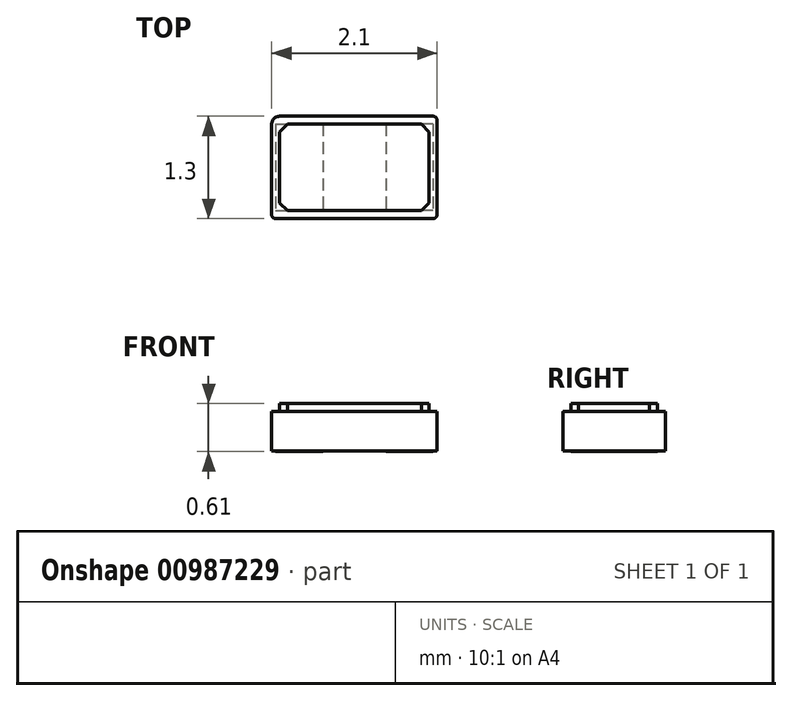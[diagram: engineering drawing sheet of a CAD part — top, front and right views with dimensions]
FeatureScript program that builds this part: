
annotation { "Feature Type Name" : "Feature", "Feature Type Description" : "" }
export const myFeature = defineFeature(function(context is Context, id is Id, definition is map)
    precondition{}
    {
        {
            var Q0;
            Q0=qCreatedBy(makeId("Top.planeOp"),FACE);
            var sketch = newSketch(context, id + "F0", { "sketchPlane" : qUnion([Q0])});
            skLineSegment(sketch, "E0.bottom", {"start": v(-0.95, 0.65) * mm, "end": v(1, 0.65) * mm});
            skLineSegment(sketch, "E0.top", {"start": v(-1, -0.65) * mm, "end": v(1, -0.65) * mm});
            skLineSegment(sketch, "E0.left", {"start": v(-1.05, 0.55) * mm, "end": v(-1.05, -0.6) * mm});
            skLineSegment(sketch, "E0.right", {"start": v(1.05, 0.6) * mm, "end": v(1.05, -0.6) * mm});
            skPoint(sketch, "E0.middle", {"position": v(0, 0) * mm});
            skPoint(sketch, "E1.visualSharp", {"position": v(-1.05, 0.65) * mm});
            skArc(sketch, "E1.filletArc", {"start": v(-0.95, 0.65) * mm, "mid": v(-1.02, 0.62) * mm, "end": v(-1.05, 0.55) * mm});
            skPoint(sketch, "E2.visualSharp", {"position": v(1.05, 0.65) * mm});
            skArc(sketch, "E2.filletArc", {"start": v(1.05, 0.6) * mm, "mid": v(1.04, 0.64) * mm, "end": v(1, 0.65) * mm});
            skPoint(sketch, "E3.visualSharp", {"position": v(-1.05, -0.65) * mm});
            skArc(sketch, "E3.filletArc", {"start": v(-1.05, -0.6) * mm, "mid": v(-1.04, -0.64) * mm, "end": v(-1, -0.65) * mm});
            skPoint(sketch, "E4.visualSharp", {"position": v(1.05, -0.65) * mm});
            skArc(sketch, "E4.filletArc", {"start": v(1, -0.65) * mm, "mid": v(1.04, -0.64) * mm, "end": v(1.05, -0.6) * mm});
            skSolve(sketch);
        }
        {
            var Q0;
            Q0=makeQuery(id+"F0.imprint","IMPRINT",FACE,{"disambiguationData":[TD([[makeQuery(id+"F0.imprint","IMPRINT",EDGE,{"derivedFrom":sQuery(id+"F0.wireOp",EDGE,"E0.bottom")}),-1.0]])]});
            extrude(context, id + "F1", {"entities" : qUnion([Q0]), "depth" : 0.5 * mm, "offsetDistance" : 25 * mm});
        }
        {
            var Q0;
            Q0=makeQuery(id+"F1.opExtrude","CAP_FACE",FACE,{"disambiguationData":[OSD([sQuery(id+"F0.wireOp",EDGE,"E0.bottom"),sQuery(id+"F0.wireOp",EDGE,"E0.top"),sQuery(id+"F0.wireOp",EDGE,"E0.left"),sQuery(id+"F0.wireOp",EDGE,"E0.right"),sQuery(id+"F0.wireOp",EDGE,"E1.filletArc"),sQuery(id+"F0.wireOp",EDGE,"E2.filletArc"),sQuery(id+"F0.wireOp",EDGE,"E3.filletArc"),sQuery(id+"F0.wireOp",EDGE,"E4.filletArc")])],"isStart":false});
            var sketch = newSketch(context, id + "F2", { "sketchPlane" : qUnion([Q0])});
            skLineSegment(sketch, "E5.0", {"start": v(-0.95, 0.65) * mm, "end": v(1, 0.65) * mm});
            skArc(sketch, "E6.0", {"start": v(-0.95, 0.65) * mm, "mid": v(-1.02, 0.62) * mm, "end": v(-1.05, 0.55) * mm});
            skLineSegment(sketch, "E7.0", {"start": v(-1.05, 0.55) * mm, "end": v(-1.05, -0.6) * mm});
            skArc(sketch, "E8.0", {"start": v(-1.05, -0.6) * mm, "mid": v(-1.04, -0.64) * mm, "end": v(-1, -0.65) * mm});
            skLineSegment(sketch, "E9.0", {"start": v(-1, -0.65) * mm, "end": v(1, -0.65) * mm});
            skArc(sketch, "E10.0", {"start": v(1, -0.65) * mm, "mid": v(1.04, -0.64) * mm, "end": v(1.05, -0.6) * mm});
            skLineSegment(sketch, "E11.0", {"start": v(1.05, 0.6) * mm, "end": v(1.05, -0.6) * mm});
            skArc(sketch, "E12.0", {"start": v(1.05, 0.6) * mm, "mid": v(1.04, 0.64) * mm, "end": v(1, 0.65) * mm});
            skLineSegment(sketch, "E13.0", {"start": v(-0.95, 0.55) * mm, "end": v(-0.95, 0.55) * mm});
            skLineSegment(sketch, "E13.1", {"start": v(-0.95, 0.55) * mm, "end": v(0.95, 0.55) * mm});
            skLineSegment(sketch, "E13.2", {"start": v(-0.95, 0.55) * mm, "end": v(-0.95, -0.55) * mm});
            skLineSegment(sketch, "E13.5", {"start": v(-0.95, -0.55) * mm, "end": v(0.95, -0.55) * mm});
            skLineSegment(sketch, "E13.7", {"start": v(0.95, 0.55) * mm, "end": v(0.95, -0.55) * mm});
            skSolve(sketch);
        }
        {
            var Q0;
            Q0=makeQuery(id+"F2.imprint","IMPRINT",FACE,{"disambiguationData":[TD([[makeQuery(id+"F2.imprint","IMPRINT",EDGE,{"derivedFrom":sQuery(id+"F2.wireOp",EDGE,"E13.1")}),-1.0]])]});
            extrude(context, id + "F3", {"entities" : qUnion([Q0]), "operationType" : NewBodyOperationType.ADD, "depth" : 0.1 * mm, "offsetDistance" : 25 * mm});
        }
        {
            var Q0;
            Q0=makeQuery(id+"F1.opExtrude","CAP_FACE",FACE,{"disambiguationData":[OSD([sQuery(id+"F0.wireOp",EDGE,"E0.bottom"),sQuery(id+"F0.wireOp",EDGE,"E0.top"),sQuery(id+"F0.wireOp",EDGE,"E0.left"),sQuery(id+"F0.wireOp",EDGE,"E0.right"),sQuery(id+"F0.wireOp",EDGE,"E1.filletArc"),sQuery(id+"F0.wireOp",EDGE,"E2.filletArc"),sQuery(id+"F0.wireOp",EDGE,"E3.filletArc"),sQuery(id+"F0.wireOp",EDGE,"E4.filletArc")])],"isStart":true});
            var sketch = newSketch(context, id + "F4", { "sketchPlane" : qUnion([Q0])});
            skLineSegment(sketch, "E14.bottom", {"start": v(1, -0.55) * mm, "end": v(0.4, -0.55) * mm});
            skLineSegment(sketch, "E14.top", {"start": v(1, 0.55) * mm, "end": v(0.4, 0.55) * mm});
            skLineSegment(sketch, "E14.left", {"start": v(1, -0.55) * mm, "end": v(1, 0.55) * mm});
            skLineSegment(sketch, "E14.right", {"start": v(0.4, -0.55) * mm, "end": v(0.4, 0.55) * mm});
            skPoint(sketch, "E14.middle", {"position": v(0.7, 0) * mm});
            skLineSegment(sketch, "E15.bottom", {"start": v(-1, -0.55) * mm, "end": v(-0.4, -0.55) * mm});
            skLineSegment(sketch, "E15.top", {"start": v(-1, 0.55) * mm, "end": v(-0.4, 0.55) * mm});
            skLineSegment(sketch, "E15.left", {"start": v(-1, -0.55) * mm, "end": v(-1, 0.55) * mm});
            skLineSegment(sketch, "E15.right", {"start": v(-0.4, -0.55) * mm, "end": v(-0.4, 0.55) * mm});
            skPoint(sketch, "E15.middle", {"position": v(-0.7, 0) * mm});
            skLineSegment(sketch, "E16", {"start": v(-0.7, 0) * mm, "end": v(0.7, 0) * mm, "construction": true});
            skLineSegment(sketch, "E17", {"start": v(0, 0) * mm, "end": v(0, 0.55) * mm, "construction": true});
            skSolve(sketch);
        }
        {
            var Q0;
            Q0 = qSketchRegion(id + "F4", true);
            extrude(context, id + "F5", {"entities" : qUnion([Q0]), "operationType" : NewBodyOperationType.ADD, "depth" : 0.01 * mm, "offsetDistance" : 25 * mm});
        }
        {
            var Q0;
            Q0=makeQuery(id+"F3.opExtrude","SWEPT_EDGE",EDGE,{"disambiguationData":[OSD([sQuery(id+"F2.wireOp",EDGE,"E13.5"),sQuery(id+"F2.wireOp",EDGE,"E13.7")])]});
            var Q1;
            Q1=makeQuery(id+"F3.opExtrude","SWEPT_EDGE",EDGE,{"disambiguationData":[OSD([sQuery(id+"F2.wireOp",EDGE,"E13.1"),sQuery(id+"F2.wireOp",EDGE,"E13.7")])]});
            var Q2;
            Q2=makeQuery(id+"F3.opExtrude","SWEPT_EDGE",EDGE,{"disambiguationData":[OSD([sQuery(id+"F2.wireOp",EDGE,"E13.1"),sQuery(id+"F2.wireOp",EDGE,"E13.2")])]});
            var Q3;
            Q3=makeQuery(id+"F3.opExtrude","SWEPT_EDGE",EDGE,{"disambiguationData":[OSD([sQuery(id+"F2.wireOp",EDGE,"E13.2"),sQuery(id+"F2.wireOp",EDGE,"E13.5")])]});
            chamfer(context, id + "F6", {"entities" : qUnion([Q0, Q1, Q2, Q3]), "width" : 0.1 * mm, "tangentPropagation" : true});
        }
    });
